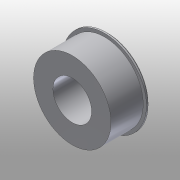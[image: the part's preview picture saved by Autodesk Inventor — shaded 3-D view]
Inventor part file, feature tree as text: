
AUTODESK INVENTOR PART (.ipt)
format: ipt  version: 2016 (Build 200138000, 138)  size: 105,984 bytes
history: native  units: mm
features: extrude x3, sketch x3, chamfer x1
ambient origin geometry x8: Origin, YZ Plane, XZ Plane, XY Plane, X Axis, Y Axis, Z Axis, Center Point
bodies: Solid1 (feature_tree)
feature tree (7):
  extrude  "Extrusion1"  Depth=5.0mm TaperAngle=0.0deg
  extrude  "Extrusion2"  Depth=0.5mm TaperAngle=0.0deg
  chamfer  "Chamfer1"  Distance=0.25mm Angle=45.0deg
  extrude  "Extrusion3"  Depth=0.5mm TaperAngle=0.0deg
  sketch  "Sketch1"  dims[d0=12.0mm d1=5.0mm d2=0.0mm]
  sketch  "Sketch2"  dims[d3=13.0mm d4=0.5mm d5=0.0mm d6=0.25mm d7=2.0mm d8=45.0deg]
  sketch  "Sketch3"  dims[d9=6.0mm d10=0.5mm d11=0.0mm]
